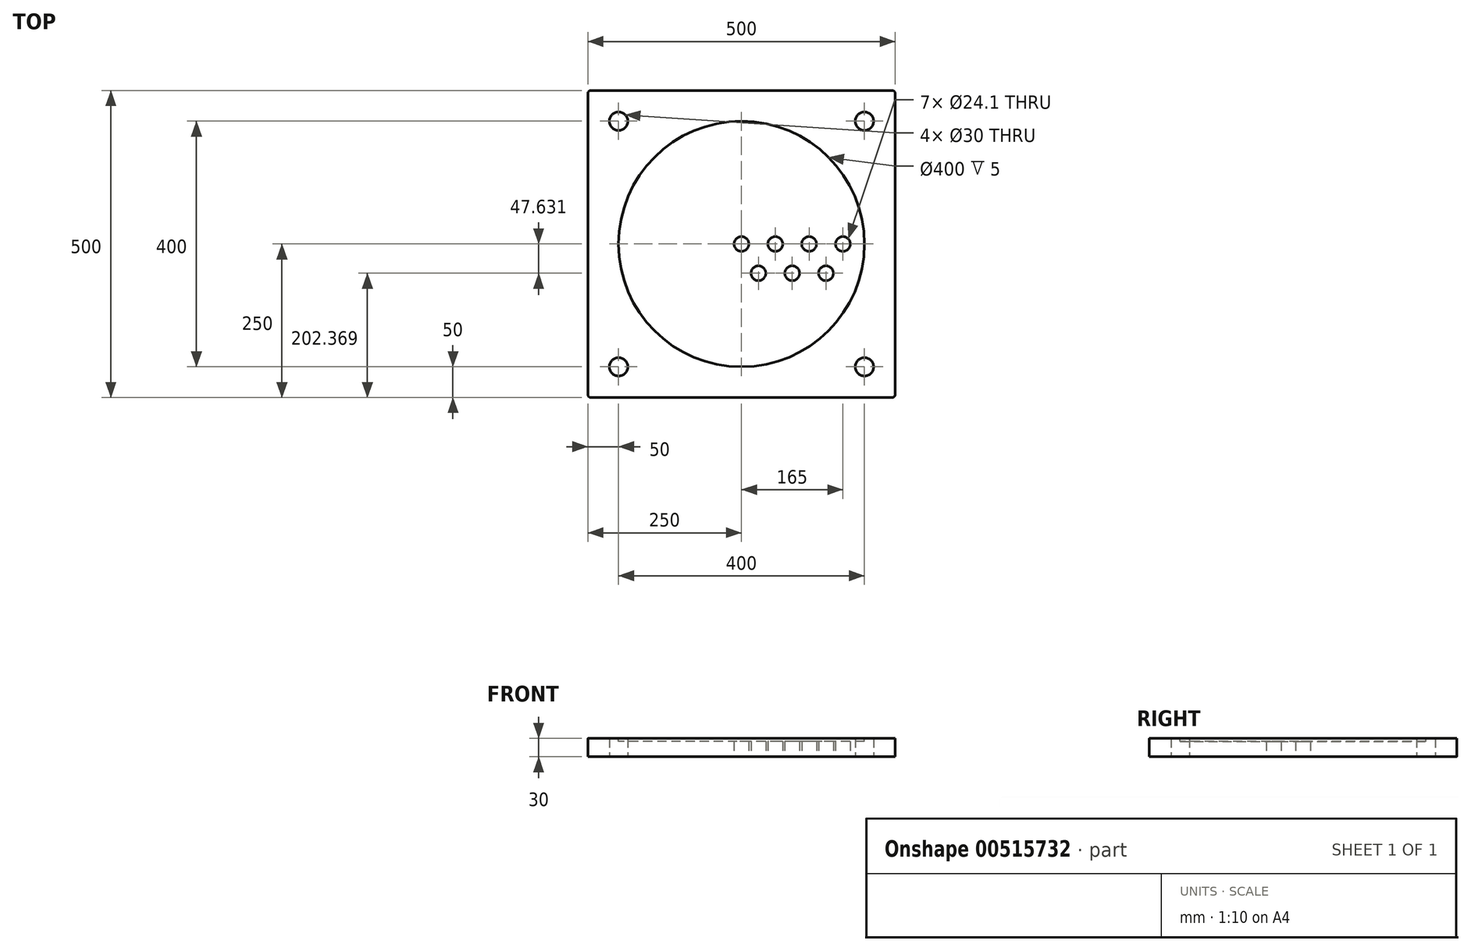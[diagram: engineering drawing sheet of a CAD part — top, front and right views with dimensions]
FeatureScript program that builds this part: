
annotation { "Feature Type Name" : "Feature", "Feature Type Description" : "" }
export const myFeature = defineFeature(function(context is Context, id is Id, definition is map)
    precondition{}
    {
        {
            var Q0;
            Q0=qCreatedBy(makeId("Top.planeOp"),FACE);
            var sketch = newSketch(context, id + "F0", { "sketchPlane" : qUnion([Q0])});
            skLineSegment(sketch, "E0.bottom", {"start": v(250, -250) * mm, "end": v(-250, -250) * mm});
            skLineSegment(sketch, "E0.top", {"start": v(250, 250) * mm, "end": v(-250, 250) * mm});
            skLineSegment(sketch, "E0.left", {"start": v(250, -250) * mm, "end": v(250, 250) * mm});
            skLineSegment(sketch, "E0.right", {"start": v(-250, -250) * mm, "end": v(-250, 250) * mm});
            skPoint(sketch, "E0.middle", {"position": v(0, 0) * mm});
            skCircle(sketch, "E1", {"center": v(200, 200) * mm, "radius": 15 * mm});
            skCircle(sketch, "E2.MirrorC", {"center": v(-200, 200) * mm, "radius": 15 * mm});
            skCircle(sketch, "E3.MirrorC", {"center": v(-200, -200) * mm, "radius": 15 * mm});
            skCircle(sketch, "E4.MirrorC", {"center": v(200, -200) * mm, "radius": 15 * mm});
            skCircle(sketch, "E5", {"center": v(0, 0) * mm, "radius": 12.05 * mm});
            skCircle(sketch, "E6.1.0.0", {"center": v(55, 0) * mm, "radius": 12.05 * mm});
            skCircle(sketch, "E6.2.0.0", {"center": v(110, 0) * mm, "radius": 12.05 * mm});
            skCircle(sketch, "E6.3.0.0", {"center": v(165, 0) * mm, "radius": 12.05 * mm});
            skLineSegment(sketch, "E6.direction1", {"start": v(0, 0) * mm, "end": v(55, 0) * mm, "construction": true});
            skCircle(sketch, "E7.1.0", {"center": v(27.5, -47.63) * mm, "radius": 12.05 * mm});
            skLineSegment(sketch, "E7.anchor2", {"start": v(0, 0) * mm, "end": v(27.5, -47.63) * mm, "construction": true});
            skCircle(sketch, "E8.1.0.0", {"center": v(82.5, -47.63) * mm, "radius": 12.05 * mm});
            skCircle(sketch, "E8.2.0.0", {"center": v(137.5, -47.63) * mm, "radius": 12.05 * mm});
            skLineSegment(sketch, "E8.direction1", {"start": v(27.5, -47.63) * mm, "end": v(82.5, -47.63) * mm, "construction": true});
            skSolve(sketch);
        }
        {
            var Q0;
            Q0=makeQuery(id+"F0.imprint","IMPRINT",FACE,{"disambiguationData":[TD([[makeQuery(id+"F0.imprint","IMPRINT",EDGE,{"derivedFrom":sQuery(id+"F0.wireOp",EDGE,"E0.bottom")}),-1.0]])]});
            extrude(context, id + "F1", {"entities" : qUnion([Q0]), "depth" : 30 * mm, "offsetDistance" : 25 * mm});
        }
        {
            var Q0;
            Q0=makeQuery(id+"F1.opExtrude","SWEPT_EDGE",EDGE,{"disambiguationData":[OSD([sQuery(id+"F0.wireOp",EDGE,"E0.bottom"),sQuery(id+"F0.wireOp",EDGE,"E0.right")])]});
            var Q1;
            Q1=makeQuery(id+"F1.opExtrude","SWEPT_EDGE",EDGE,{"disambiguationData":[OSD([sQuery(id+"F0.wireOp",EDGE,"E0.bottom"),sQuery(id+"F0.wireOp",EDGE,"E0.left")])]});
            var Q2;
            Q2=makeQuery(id+"F1.opExtrude","SWEPT_EDGE",EDGE,{"disambiguationData":[OSD([sQuery(id+"F0.wireOp",EDGE,"E0.top"),sQuery(id+"F0.wireOp",EDGE,"E0.left")])]});
            var Q3;
            Q3=makeQuery(id+"F1.opExtrude","SWEPT_EDGE",EDGE,{"disambiguationData":[OSD([sQuery(id+"F0.wireOp",EDGE,"E0.top"),sQuery(id+"F0.wireOp",EDGE,"E0.right")])]});
            fillet(context, id + "F2", {"entities" : qUnion([Q0, Q1, Q2, Q3]), "radius" : 5 * mm, "tangentPropagation" : true, "allowEdgeOverflow" : false});
        }
        {
            var Q0;
            Q0=makeQuery(id+"F1.opExtrude","CAP_FACE",FACE,{"disambiguationData":[OSD([sQuery(id+"F0.wireOp",EDGE,"E0.bottom"),sQuery(id+"F0.wireOp",EDGE,"E0.top"),sQuery(id+"F0.wireOp",EDGE,"E0.left"),sQuery(id+"F0.wireOp",EDGE,"E0.right")])],"isStart":false});
            var sketch = newSketch(context, id + "F3", { "sketchPlane" : qUnion([Q0])});
            skCircle(sketch, "E9", {"center": v(0, 0) * mm, "radius": 200 * mm});
            skSolve(sketch);
        }
        {
            var Q0;
            Q0 = qSketchRegion(id + "F3", true);
            extrude(context, id + "F4", {"entities" : qUnion([Q0]), "operationType" : NewBodyOperationType.REMOVE, "oppositeDirection" : true, "depth" : 5 * mm, "offsetDistance" : 25 * mm});
        }
    });
